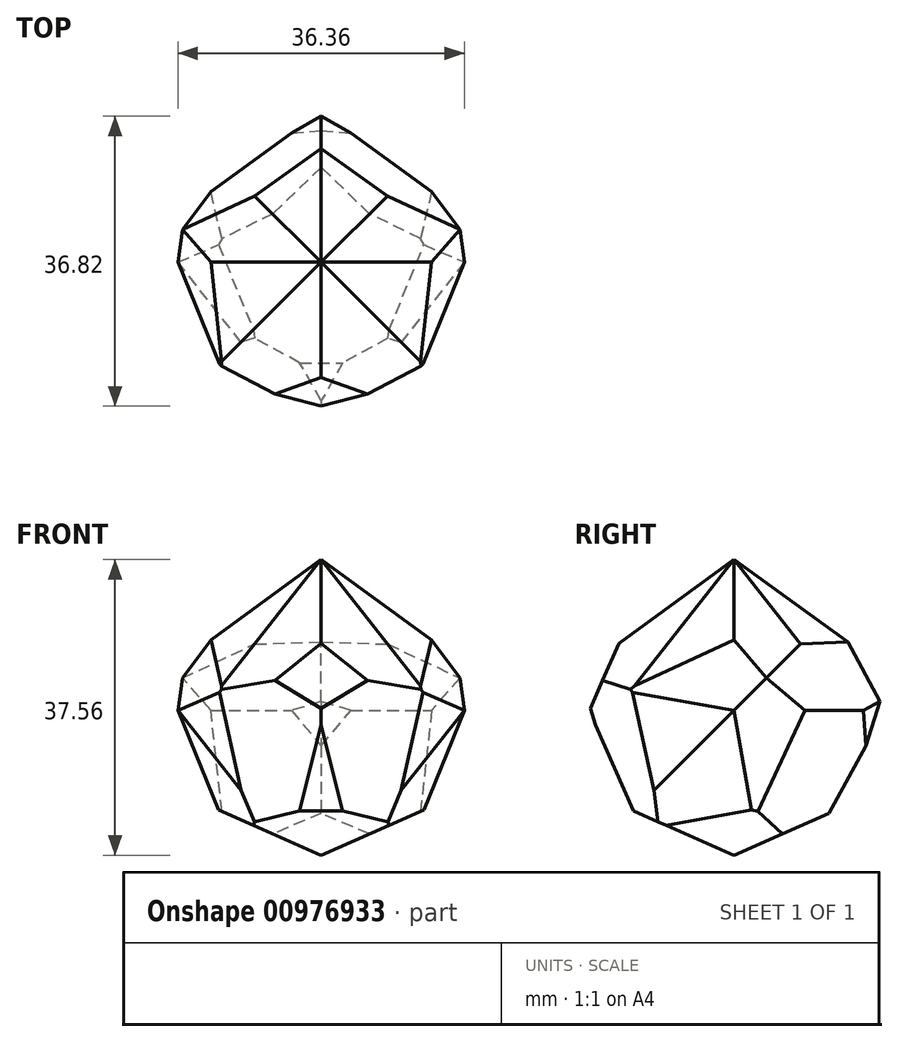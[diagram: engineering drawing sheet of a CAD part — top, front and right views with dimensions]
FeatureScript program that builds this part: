
annotation { "Feature Type Name" : "Feature", "Feature Type Description" : "" }
export const myFeature = defineFeature(function(context is Context, id is Id, definition is map)
    precondition{}
    {
        {
            var Q0;
            Q0=qCreatedBy(makeId("Front.planeOp"),FACE);
            var sketch = newSketch(context, id + "F0", { "sketchPlane" : qUnion([Q0])});
            skCircle(sketch, "E0.cCircle", {"center": v(0, 16.8) * mm, "radius": 16.8 * mm, "construction": true});
            skLineSegment(sketch, "E0.0", {"start": v(12.2, 0) * mm, "end": v(-12.2, 0) * mm});
            skLineSegment(sketch, "E0.1", {"start": v(-12.2, 0) * mm, "end": v(-19.75, 23.21) * mm});
            skLineSegment(sketch, "E0.2", {"start": v(-19.75, 23.21) * mm, "end": v(0, 37.56) * mm});
            skLineSegment(sketch, "E0.3", {"start": v(0, 37.56) * mm, "end": v(19.75, 23.21) * mm});
            skLineSegment(sketch, "E0.4", {"start": v(19.75, 23.21) * mm, "end": v(12.2, 0) * mm});
            skPoint(sketch, "E0.0.midPoint", {"position": v(0, 0) * mm});
            skSolve(sketch);
        }
        {
            var Q0;
            Q0=qCreatedBy(makeId("Right.planeOp"),FACE);
            var sketch = newSketch(context, id + "F1", { "sketchPlane" : qUnion([Q0])});
            skLineSegment(sketch, "E1", {"start": v(0, 16.79) * mm, "end": v(38.1, 16.79) * mm});
            skLineSegment(sketch, "E2", {"start": v(38.1, 16.79) * mm, "end": v(0, 0) * mm});
            skLineSegment(sketch, "E3", {"start": v(0, 0) * mm, "end": v(0, 16.79) * mm});
            skSolve(sketch);
        }
        {
            var Q0;
            Q0=makeQuery(id+"F0.imprint","IMPRINT",FACE,{"disambiguationData":[TD([[makeQuery(id+"F0.imprint","IMPRINT",EDGE,{"derivedFrom":sQuery(id+"F0.wireOp",EDGE,"E0.0")}),-1.0]])]});
            var Q1;
            Q1=sQuery(id+"F1.wireOp",VERTEX,"E1.end");
            loft(context, id + "F2", {"sheetProfilesArray" : [{ "sheetProfileEntities" : qUnion([Q0]) }, { "sheetProfileEntities" : qUnion([Q1]) }]});
        }
        {
            var Q0;
            Q0=qCreatedBy(makeId("Front.planeOp"),FACE);
            var sketch = newSketch(context, id + "F3", { "sketchPlane" : qUnion([Q0])});
            skLineSegment(sketch, "E4", {"start": v(0, 0) * mm, "end": v(0, 36.78) * mm});
            skLineSegment(sketch, "E5", {"start": v(0, 36.78) * mm, "end": v(0, 18.4) * mm});
            skLineSegment(sketch, "E6", {"start": v(0, 18.4) * mm, "end": v(18.44, 18.4) * mm});
            skLineSegment(sketch, "E7", {"start": v(18.44, 18.4) * mm, "end": v(-18.2, 18.4) * mm});
            skSolve(sketch);
        }
        {
            var Q0;
            Q0=makeQuery(id+"F2.opLoft","SWEPT_BODY",BODY,{"disambiguationData":[OSD([makeQuery(id+"F0.imprint","IMPRINT",FACE,{"disambiguationData":[TD([[makeQuery(id+"F0.imprint","IMPRINT",EDGE,{"derivedFrom":sQuery(id+"F0.wireOp",EDGE,"E0.0")}),-1.0]])]}),sQuery(id+"F1.wireOp",VERTEX,"E1.end")])]});
            var Q1;
            Q1=qCreatedBy(makeId("Front.planeOp"),FACE);
            mirror(context, id + "F4", {"operationType" : NewBodyOperationType.ADD, "entities" : qUnion([Q0]), "mirrorPlane" : qUnion([Q1])});
        }
        {
            var Q0;
            Q0=makeQuery(id+"F2.opLoft","SWEPT_BODY",BODY,{"disambiguationData":[OSD([makeQuery(id+"F0.imprint","IMPRINT",FACE,{"disambiguationData":[TD([[makeQuery(id+"F0.imprint","IMPRINT",EDGE,{"derivedFrom":sQuery(id+"F0.wireOp",EDGE,"E0.0")}),-1.0]])]}),sQuery(id+"F1.wireOp",VERTEX,"E1.end")])]});
            var Q1;
            Q1=sQuery(id+"F3.wireOp",EDGE,"E4");
            circularPattern(context, id + "F5", {"entities" : qUnion([Q0]), "axis" : qUnion([Q1]), "angle" : 360 * degree, "instanceCount" : 4, "equalSpace" : true});
        }
        {
            var Q0;
            Q0=makeQuery(id+"F2.opLoft","SWEPT_BODY",BODY,{"disambiguationData":[OSD([makeQuery(id+"F0.imprint","IMPRINT",FACE,{"disambiguationData":[TD([[makeQuery(id+"F0.imprint","IMPRINT",EDGE,{"derivedFrom":sQuery(id+"F0.wireOp",EDGE,"E0.0")}),-1.0]])]}),sQuery(id+"F1.wireOp",VERTEX,"E1.end")])]});
            var Q1;
            Q1=sQuery(id+"F3.wireOp",EDGE,"E7");
            circularPattern(context, id + "F6", {"entities" : qUnion([Q0]), "axis" : qUnion([Q1]), "angle" : 90 * degree, "instanceCount" : 2, "equalSpace" : true});
        }
        {
            var Q0;
            Q0=makeQuery(id+"F2.opLoft","SWEPT_BODY",BODY,{"disambiguationData":[OSD([makeQuery(id+"F0.imprint","IMPRINT",FACE,{"disambiguationData":[TD([[makeQuery(id+"F0.imprint","IMPRINT",EDGE,{"derivedFrom":sQuery(id+"F0.wireOp",EDGE,"E0.0")}),-1.0]])]}),sQuery(id+"F1.wireOp",VERTEX,"E1.end")])]});
            var Q1;
            Q1=makeQuery(id+"F5.opPattern","COPY",BODY,{"derivedFrom":makeQuery(id+"F2.opLoft","SWEPT_BODY",BODY,{"disambiguationData":[OSD([makeQuery(id+"F0.imprint","IMPRINT",FACE,{"disambiguationData":[TD([[makeQuery(id+"F0.imprint","IMPRINT",EDGE,{"derivedFrom":sQuery(id+"F0.wireOp",EDGE,"E0.0")}),-1.0]])]}),sQuery(id+"F1.wireOp",VERTEX,"E1.end")])]}),"instanceName":"1"});
            var Q2;
            Q2=makeQuery(id+"F6.opPattern","COPY",BODY,{"derivedFrom":makeQuery(id+"F2.opLoft","SWEPT_BODY",BODY,{"disambiguationData":[OSD([makeQuery(id+"F0.imprint","IMPRINT",FACE,{"disambiguationData":[TD([[makeQuery(id+"F0.imprint","IMPRINT",EDGE,{"derivedFrom":sQuery(id+"F0.wireOp",EDGE,"E0.0")}),-1.0]])]}),sQuery(id+"F1.wireOp",VERTEX,"E1.end")])]}),"instanceName":"1"});
            var Q3;
            Q3=makeQuery(id+"F5.opPattern","COPY",BODY,{"derivedFrom":makeQuery(id+"F2.opLoft","SWEPT_BODY",BODY,{"disambiguationData":[OSD([makeQuery(id+"F0.imprint","IMPRINT",FACE,{"disambiguationData":[TD([[makeQuery(id+"F0.imprint","IMPRINT",EDGE,{"derivedFrom":sQuery(id+"F0.wireOp",EDGE,"E0.0")}),-1.0]])]}),sQuery(id+"F1.wireOp",VERTEX,"E1.end")])]}),"instanceName":"2"});
            var Q4;
            Q4=makeQuery(id+"F5.opPattern","COPY",BODY,{"derivedFrom":makeQuery(id+"F2.opLoft","SWEPT_BODY",BODY,{"disambiguationData":[OSD([makeQuery(id+"F0.imprint","IMPRINT",FACE,{"disambiguationData":[TD([[makeQuery(id+"F0.imprint","IMPRINT",EDGE,{"derivedFrom":sQuery(id+"F0.wireOp",EDGE,"E0.0")}),-1.0]])]}),sQuery(id+"F1.wireOp",VERTEX,"E1.end")])]}),"instanceName":"3"});
            booleanBodies(context, id + "F7", {"operationType" : BooleanOperationType.INTERSECTION, "tools" : qUnion([Q0, Q1, Q2, Q3, Q4])});
        }
    });
